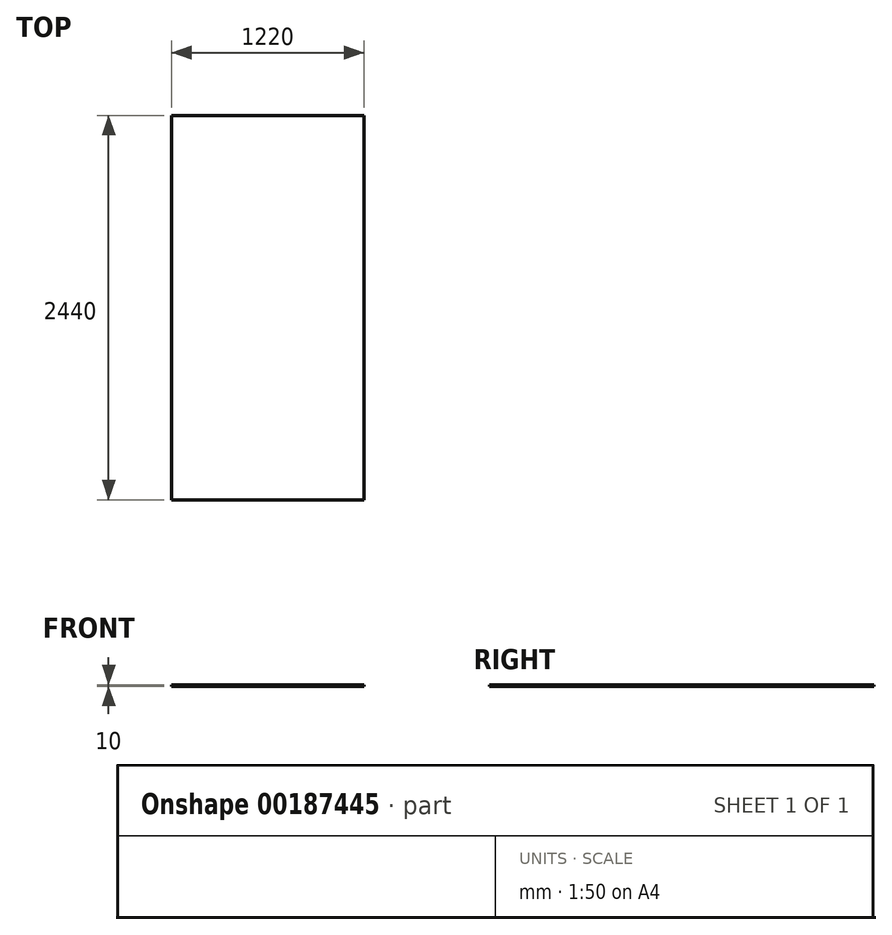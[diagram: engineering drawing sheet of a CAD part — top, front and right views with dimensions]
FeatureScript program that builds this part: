
annotation { "Feature Type Name" : "Feature", "Feature Type Description" : "" }
export const myFeature = defineFeature(function(context is Context, id is Id, definition is map)
    precondition{}
    {
        {
            var Q0;
            Q0=qCreatedBy(makeId("Top.planeOp"),FACE);
            var sketch = newSketch(context, id + "F0", { "sketchPlane" : qUnion([Q0])});
            skLineSegment(sketch, "E0.bottom", {"start": v(-606.12, 1797.74) * mm, "end": v(613.88, 1797.74) * mm});
            skLineSegment(sketch, "E0.top", {"start": v(-606.12, -642.26) * mm, "end": v(613.88, -642.26) * mm});
            skLineSegment(sketch, "E0.left", {"start": v(-606.12, 1797.74) * mm, "end": v(-606.12, -642.26) * mm});
            skLineSegment(sketch, "E0.right", {"start": v(613.88, 1797.74) * mm, "end": v(613.88, -642.26) * mm});
            skSolve(sketch);
        }
        {
            var Q0;
            Q0=makeQuery(id+"F0.imprint","IMPRINT",FACE,{"disambiguationData":[TD([[makeQuery(id+"F0.imprint","IMPRINT",EDGE,{"derivedFrom":sQuery(id+"F0.wireOp",EDGE,"E0.bottom")}),-1.0]])]});
            extrude(context, id + "F1", {"entities" : qUnion([Q0]), "depth" : 10 * mm});
        }
    });
